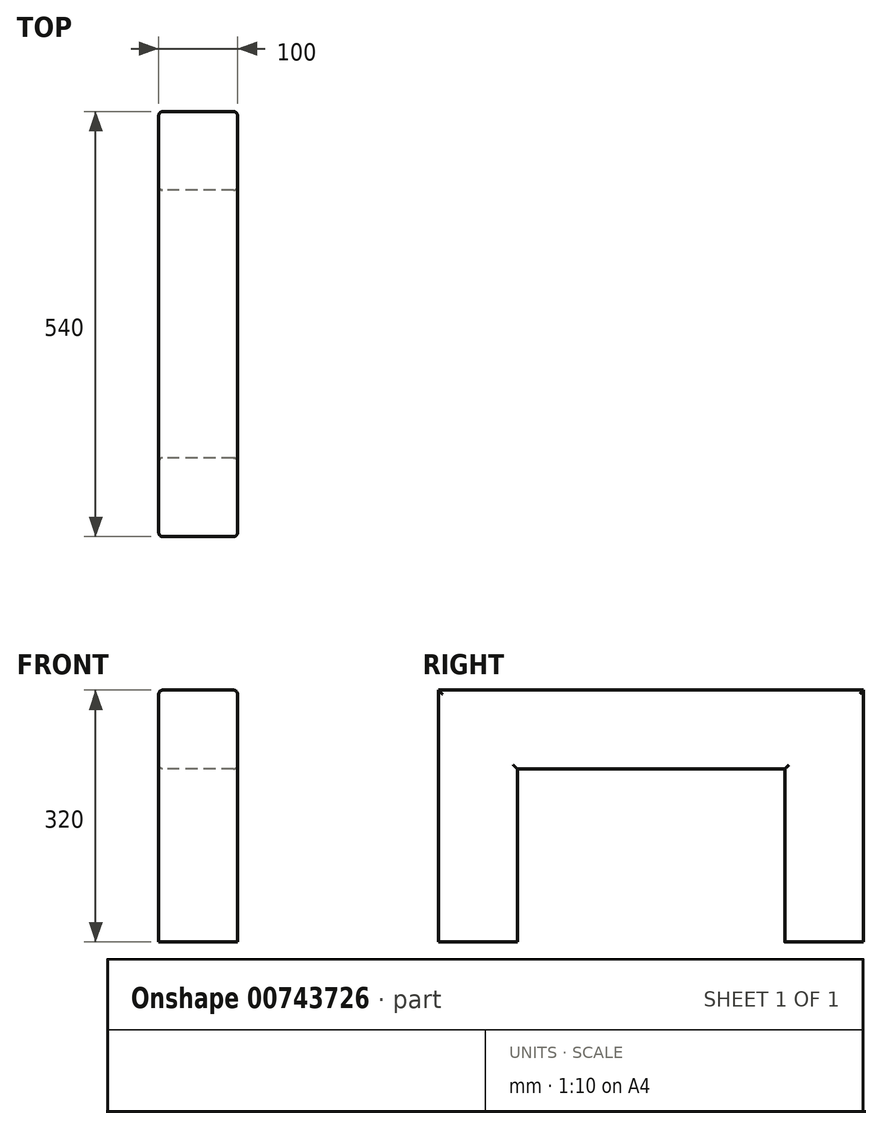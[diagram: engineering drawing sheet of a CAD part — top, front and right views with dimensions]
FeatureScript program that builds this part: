
annotation { "Feature Type Name" : "Feature", "Feature Type Description" : "" }
export const myFeature = defineFeature(function(context is Context, id is Id, definition is map)
    precondition{}
    {
        {
            var Q0;
            Q0=qCreatedBy(makeId("Right.planeOp"),FACE);
            var sketch = newSketch(context, id + "F0", { "sketchPlane" : qUnion([Q0])});
            skLineSegment(sketch, "E0", {"start": v(0, 0) * mm, "end": v(0, 220) * mm});
            skLineSegment(sketch, "E1", {"start": v(0, 220) * mm, "end": v(-340, 220) * mm});
            skLineSegment(sketch, "E2", {"start": v(-340, 220) * mm, "end": v(-340, 0) * mm});
            skLineSegment(sketch, "E3", {"start": v(-340, 0) * mm, "end": v(-440, 0) * mm});
            skLineSegment(sketch, "E4", {"start": v(-440, 0) * mm, "end": v(-440, 320) * mm});
            skLineSegment(sketch, "E5", {"start": v(-440, 320) * mm, "end": v(100, 320) * mm});
            skLineSegment(sketch, "E6", {"start": v(100, 320) * mm, "end": v(100, 0) * mm});
            skLineSegment(sketch, "E7", {"start": v(100, 0) * mm, "end": v(0, 0) * mm});
            skSolve(sketch);
        }
        {
            var Q0;
            Q0=qSketchRegion(id+"F0",true);
            extrude(context, id + "F1", {"entities" : qUnion([Q0]), "depth" : 100 * mm, "offsetDistance" : 25 * mm});
        }
        {
            var Q0;
            Q0=makeQuery(id+"F1.opExtrude","CAP_EDGE",EDGE,{"disambiguationData":[OSD([sQuery(id+"F0.wireOp",EDGE,"E4")])],"isStart":false});
            var Q1;
            Q1=makeQuery(id+"F1.opExtrude","CAP_EDGE",EDGE,{"disambiguationData":[OSD([sQuery(id+"F0.wireOp",EDGE,"E2")])],"isStart":false});
            var Q2;
            Q2=makeQuery(id+"F1.opExtrude","CAP_EDGE",EDGE,{"disambiguationData":[OSD([sQuery(id+"F0.wireOp",EDGE,"E1")])],"isStart":false});
            var Q3;
            Q3=makeQuery(id+"F1.opExtrude","CAP_EDGE",EDGE,{"disambiguationData":[OSD([sQuery(id+"F0.wireOp",EDGE,"E0")])],"isStart":false});
            var Q4;
            Q4=makeQuery(id+"F1.opExtrude","CAP_EDGE",EDGE,{"disambiguationData":[OSD([sQuery(id+"F0.wireOp",EDGE,"E6")])],"isStart":false});
            var Q5;
            Q5=makeQuery(id+"F1.opExtrude","CAP_EDGE",EDGE,{"disambiguationData":[OSD([sQuery(id+"F0.wireOp",EDGE,"E4")])],"isStart":true});
            var Q6;
            Q6=makeQuery(id+"F1.opExtrude","CAP_EDGE",EDGE,{"disambiguationData":[OSD([sQuery(id+"F0.wireOp",EDGE,"E0")])],"isStart":true});
            var Q7;
            Q7=makeQuery(id+"F1.opExtrude","CAP_EDGE",EDGE,{"disambiguationData":[OSD([sQuery(id+"F0.wireOp",EDGE,"E1")])],"isStart":true});
            var Q8;
            Q8=makeQuery(id+"F1.opExtrude","CAP_EDGE",EDGE,{"disambiguationData":[OSD([sQuery(id+"F0.wireOp",EDGE,"E2")])],"isStart":true});
            var Q9;
            Q9=makeQuery(id+"F1.opExtrude","CAP_EDGE",EDGE,{"disambiguationData":[OSD([sQuery(id+"F0.wireOp",EDGE,"E6")])],"isStart":true});
            var Q10;
            Q10=makeQuery(id+"F1.opExtrude","CAP_EDGE",EDGE,{"disambiguationData":[OSD([sQuery(id+"F0.wireOp",EDGE,"E5")])],"isStart":true});
            var Q11;
            Q11=makeQuery(id+"F1.opExtrude","CAP_EDGE",EDGE,{"disambiguationData":[OSD([sQuery(id+"F0.wireOp",EDGE,"E5")])],"isStart":false});
            fillet(context, id + "F2", {"entities" : qUnion([Q0, Q1, Q2, Q3, Q4, Q5, Q6, Q7, Q8, Q9, Q10, Q11]), "radius" : 5 * mm, "tangentPropagation" : true, "allowEdgeOverflow" : false});
        }
    });
